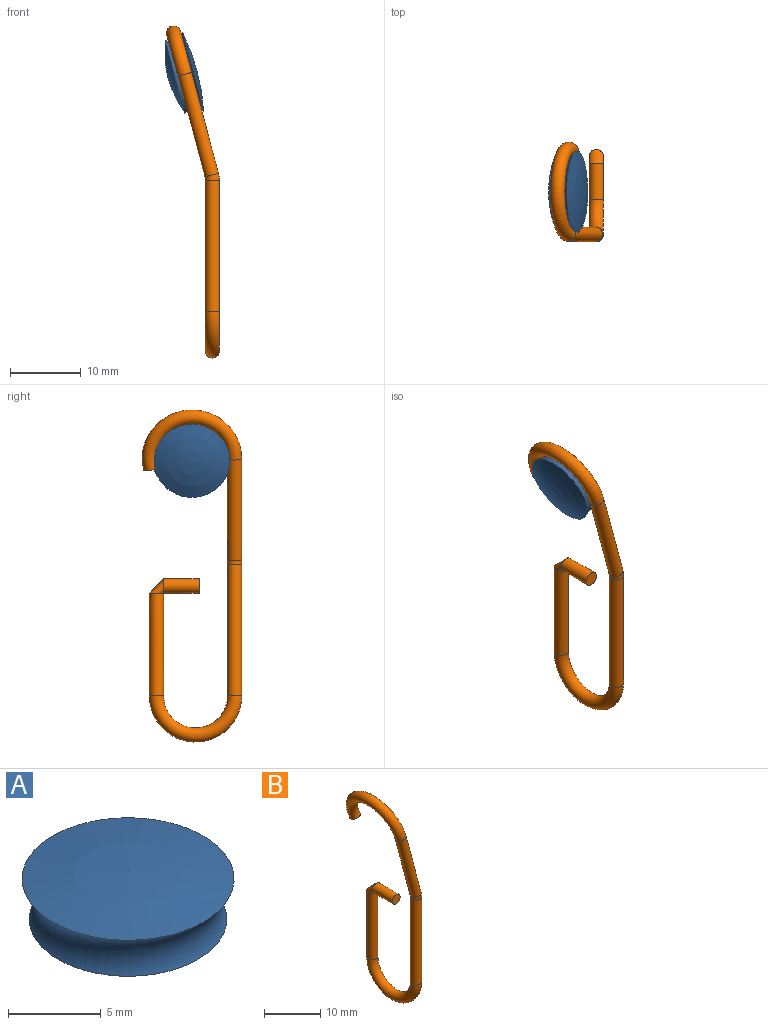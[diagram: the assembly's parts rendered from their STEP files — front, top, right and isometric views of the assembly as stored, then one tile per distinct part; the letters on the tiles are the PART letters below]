
ASSEMBLY  parts=2 mates=1
PART A: 3 faces, bbox 15.2x15.2x4.2 mm
  f0: sphere r=30mm, area 104.2mm2, adj f1
  f1: torus R=7mm, axis (0,0,1), area 96.4mm2, adj f0,f2
  f2: sphere r=15mm, area 92.7mm2, adj f1
PART B: 10 faces, bbox 6.9x15.2x47.9 mm
  f0: plane 2x2mm, normal (0,-1,0), area 3.1mm2, adj f2
  f1: plane 1.94x1.94mm, normal (0.25,-0.25,-0.94), area 3.1mm2, adj f9
  f2: cylinder r=1mm len=5mm, axis (0,1,0), area 31.4mm2, adj f0,f3
  f3: torus R=1mm, axis (-1,0,0), area 9.9mm2, adj f2,f4
  f4: cylinder r=1mm len=14.5mm, axis (0,0,-1), area 91.1mm2, adj f3,f5
  f5: torus R=5.5mm, axis (-1,0,0), area 108.6mm2, adj f4,f6
  f6: cylinder r=1mm len=18.5mm, axis (0,0,1), area 116.2mm2, adj f5,f7
  f7: torus R=3mm, axis (0,-1,0), area 4.9mm2, adj f6,f8
  f8: cylinder r=1mm len=14.74mm, axis (-0.26,0,0.97), area 92.5mm2, adj f7,f9
  f9: torus R=6mm, axis (-0.97,0,-0.26), area 128mm2, adj f1,f8
PLACE A rot(axis=(0,1,0),75deg) t=(-6.22,1,17.38)mm
PLACE B at identity fixed
MATE fastened A.f1 <-> B.f9  axis (0.97,0,0.26) through (-3.91,1,18)mm
